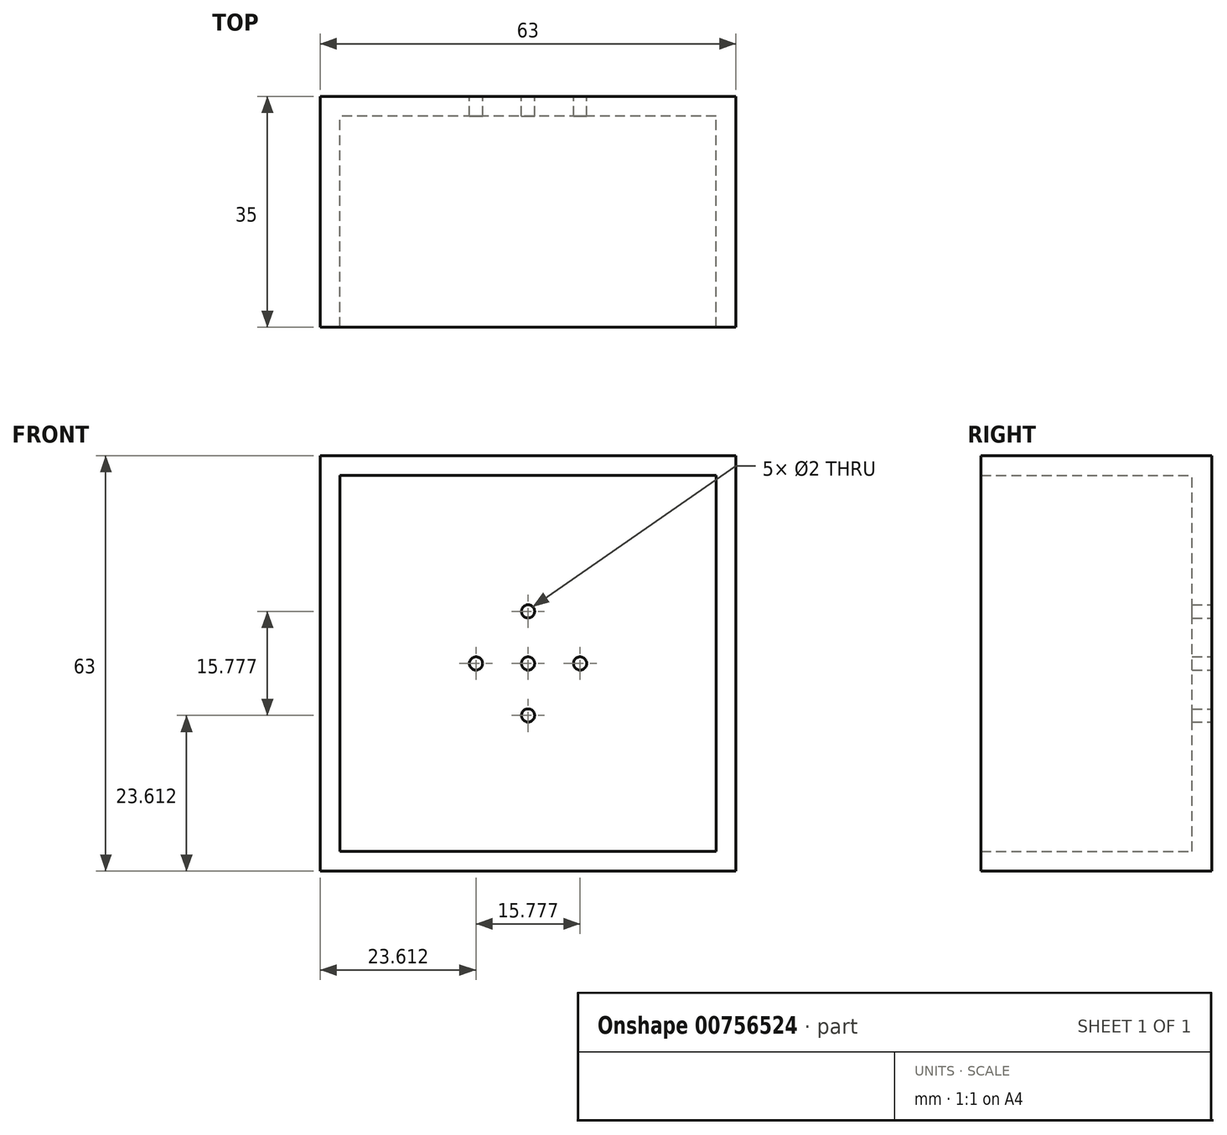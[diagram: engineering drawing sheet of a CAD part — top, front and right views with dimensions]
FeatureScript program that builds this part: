
annotation { "Feature Type Name" : "Feature", "Feature Type Description" : "" }
export const myFeature = defineFeature(function(context is Context, id is Id, definition is map)
    precondition{}
    {
        {
            var Q0;
            Q0=qCreatedBy(makeId("Front.planeOp"),FACE);
            var sketch = newSketch(context, id + "F0", { "sketchPlane" : qUnion([Q0])});
            skLineSegment(sketch, "E0.bottom", {"start": v(31.5, -31.5) * mm, "end": v(-31.5, -31.5) * mm});
            skLineSegment(sketch, "E0.top", {"start": v(31.5, 31.5) * mm, "end": v(-31.5, 31.5) * mm});
            skLineSegment(sketch, "E0.left", {"start": v(31.5, -31.5) * mm, "end": v(31.5, 31.5) * mm});
            skLineSegment(sketch, "E0.right", {"start": v(-31.5, -31.5) * mm, "end": v(-31.5, 31.5) * mm});
            skPoint(sketch, "E0.middle", {"position": v(0, 0) * mm});
            skSolve(sketch);
        }
        {
            var Q0;
            Q0 = qSketchRegion(id + "F0", true);
            extrude(context, id + "F1", {"entities" : qUnion([Q0]), "depth" : 35 * mm, "offsetDistance" : 25 * mm});
        }
        {
            var Q0;
            Q0=makeQuery(id+"F1.opExtrude","CAP_FACE",FACE,{"disambiguationData":[OSD([sQuery(id+"F0.wireOp",EDGE,"E0.bottom"),sQuery(id+"F0.wireOp",EDGE,"E0.top"),sQuery(id+"F0.wireOp",EDGE,"E0.left"),sQuery(id+"F0.wireOp",EDGE,"E0.right")])],"isStart":false});
            shell(context, id + "F2", {"entities" : qUnion([Q0]), "thickness" : 3 * mm});
        }
        {
            var Q0;
            Q0=makeQuery(id+"F1.opExtrude","CAP_FACE",FACE,{"disambiguationData":[OSD([sQuery(id+"F0.wireOp",EDGE,"E0.bottom"),sQuery(id+"F0.wireOp",EDGE,"E0.top"),sQuery(id+"F0.wireOp",EDGE,"E0.left"),sQuery(id+"F0.wireOp",EDGE,"E0.right")])],"isStart":true});
            var sketch = newSketch(context, id + "F3", { "sketchPlane" : qUnion([Q0])});
            skSolve(sketch);
        }
        {
            var Q0;
            Q0=qCreatedBy(makeId("Front.planeOp"),FACE);
            var sketch = newSketch(context, id + "F4", { "sketchPlane" : qUnion([Q0])});
            skCircle(sketch, "E1", {"center": v(7.89, 0) * mm, "radius": 1 * mm});
            skCircle(sketch, "E2", {"center": v(-7.89, 0) * mm, "radius": 1 * mm});
            skCircle(sketch, "E3", {"center": v(0, 7.89) * mm, "radius": 1 * mm});
            skCircle(sketch, "E4", {"center": v(0, -7.89) * mm, "radius": 1 * mm});
            skCircle(sketch, "E5", {"center": v(0, 0) * mm, "radius": 1 * mm});
            skSolve(sketch);
        }
        {
            var Q0;
            Q0 = qSketchRegion(id + "F4", true);
            extrude(context, id + "F5", {"entities" : qUnion([Q0]), "operationType" : NewBodyOperationType.REMOVE, "depth" : 25 * mm, "offsetDistance" : 25 * mm});
        }
    });
